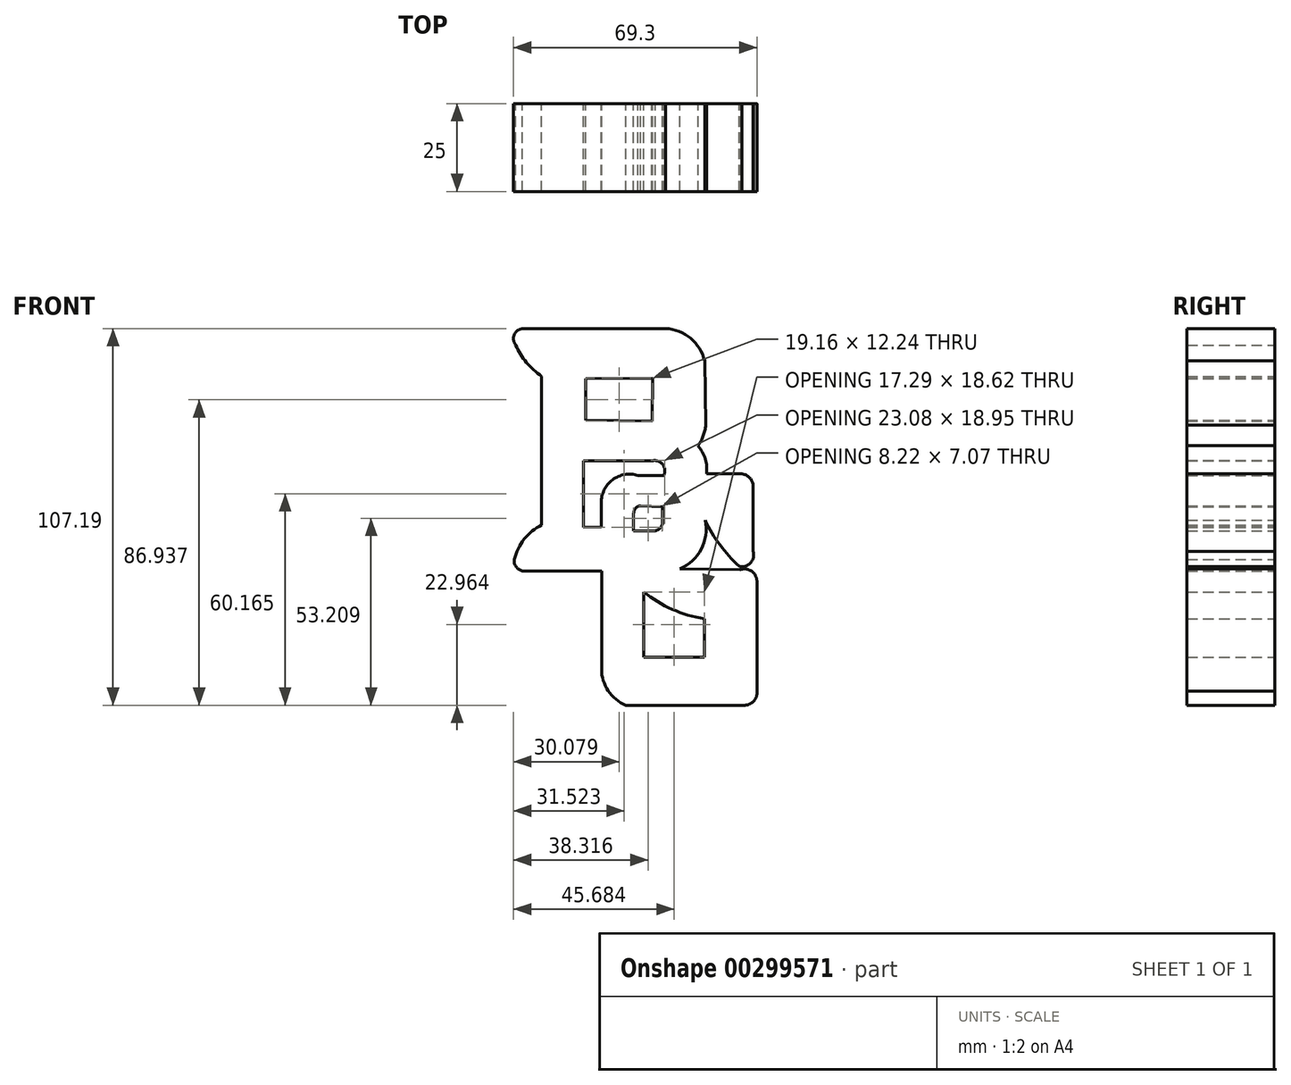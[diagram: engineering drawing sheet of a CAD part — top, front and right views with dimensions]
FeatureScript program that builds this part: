
annotation { "Feature Type Name" : "Feature", "Feature Type Description" : "" }
export const myFeature = defineFeature(function(context is Context, id is Id, definition is map)
    precondition{}
    {
        {
            var Q0;
            Q0=qCreatedBy(makeId("Front.planeOp"),FACE);
            var sketch = newSketch(context, id + "F0", { "sketchPlane" : qUnion([Q0])});
            skLineSegment(sketch, "E0", {"start": v(-27.36, 42.93) * mm, "end": v(-27.36, 0) * mm});
            skArc(sketch, "E1", {"start": v(-27.36, 0.63) * mm, "mid": v(-32.34, -3.42) * mm, "end": v(-35.18, -9.18) * mm});
            skArc(sketch, "E2", {"start": v(-35.18, -9.18) * mm, "mid": v(-34.67, -11.27) * mm, "end": v(-32.9, -12.48) * mm});
            skLineSegment(sketch, "E3", {"start": v(-32.9, -12.48) * mm, "end": v(-10.33, -12.48) * mm});
            skLineSegment(sketch, "E4", {"start": v(-10.33, -12.48) * mm, "end": v(-10.33, -40.36) * mm});
            skArc(sketch, "E5", {"start": v(-10.33, -40.36) * mm, "mid": v(-8.44, -46.58) * mm, "end": v(-3.41, -50.69) * mm});
            skLineSegment(sketch, "E6", {"start": v(-3.41, -50.69) * mm, "end": v(30.33, -50.69) * mm});
            skArc(sketch, "E7", {"start": v(30.33, -50.69) * mm, "mid": v(33.01, -49.48) * mm, "end": v(33.87, -46.66) * mm});
            skLineSegment(sketch, "E8", {"start": v(33.87, -46.66) * mm, "end": v(33.87, -15.42) * mm});
            skArc(sketch, "E9", {"start": v(33.87, -15.42) * mm, "mid": v(32.37, -12.54) * mm, "end": v(29.15, -12.12) * mm});
            skLineSegment(sketch, "E10", {"start": v(29.15, -12.12) * mm, "end": v(11.94, -11.88) * mm});
            skArc(sketch, "E11", {"start": v(11.94, -11.88) * mm, "mid": v(18.05, -6.3) * mm, "end": v(19.13, 1.91) * mm});
            skArc(sketch, "E12", {"start": v(19.13, 1.91) * mm, "mid": v(23.35, -5.06) * mm, "end": v(28.8, -11.14) * mm});
            skLineSegment(sketch, "E13", {"start": v(32.79, -6.95) * mm, "end": v(32.79, 11.61) * mm});
            skArc(sketch, "E14", {"start": v(32.79, 11.61) * mm, "mid": v(31.9, 13.96) * mm, "end": v(29.67, 15.13) * mm});
            skLineSegment(sketch, "E15", {"start": v(29.67, 15.13) * mm, "end": v(19.53, 15.13) * mm});
            skArc(sketch, "E16", {"start": v(19.53, 15.13) * mm, "mid": v(19.19, 19.39) * mm, "end": v(17.13, 23.14) * mm});
            skArc(sketch, "E17", {"start": v(17.13, 23.14) * mm, "mid": v(18.6, 25.95) * mm, "end": v(19.37, 29.03) * mm});
            skLineSegment(sketch, "E18", {"start": v(19.37, 29.03) * mm, "end": v(19.01, 47.3) * mm});
            skArc(sketch, "E19", {"start": v(19.01, 47.3) * mm, "mid": v(14.99, 53.73) * mm, "end": v(7.93, 56.5) * mm});
            skLineSegment(sketch, "E20", {"start": v(7.93, 56.5) * mm, "end": v(-32.51, 56.5) * mm});
            skArc(sketch, "E21", {"start": v(-32.51, 56.5) * mm, "mid": v(-35.12, 54.85) * mm, "end": v(-34.75, 51.79) * mm});
            skArc(sketch, "E22", {"start": v(-34.75, 51.79) * mm, "mid": v(-31.69, 46.83) * mm, "end": v(-27.36, 42.93) * mm});
            skLineSegment(sketch, "E23", {"start": v(-14.9, 42.2) * mm, "end": v(-14.9, 30.38) * mm});
            skLineSegment(sketch, "E24", {"start": v(-14.9, 30.38) * mm, "end": v(4.03, 30.13) * mm});
            skLineSegment(sketch, "E25", {"start": v(4.03, 30.13) * mm, "end": v(4.26, 42.37) * mm});
            skLineSegment(sketch, "E26", {"start": v(4.26, 42.37) * mm, "end": v(-14.9, 42.2) * mm});
            skLineSegment(sketch, "E27", {"start": v(-12.42, 10.1) * mm, "end": v(-12.49, 16.09) * mm});
            skLineSegment(sketch, "E28", {"start": v(-12.49, 16.09) * mm, "end": v(-6.72, 16.15) * mm});
            skArc(sketch, "E29", {"start": v(-6.72, 16.15) * mm, "mid": v(-10.19, 13.7) * mm, "end": v(-12.42, 10.1) * mm});
            skLineSegment(sketch, "E30", {"start": v(1.64, -18.42) * mm, "end": v(1.64, -37.03) * mm});
            skLineSegment(sketch, "E31", {"start": v(1.64, -37.03) * mm, "end": v(18.93, -37.03) * mm});
            skLineSegment(sketch, "E32", {"start": v(18.93, -37.03) * mm, "end": v(18.93, -26.1) * mm});
            skArc(sketch, "E33", {"start": v(1.64, -18.42) * mm, "mid": v(9.78, -23.39) * mm, "end": v(18.93, -26.1) * mm});
            skLineSegment(sketch, "E34", {"start": v(7.01, 5.83) * mm, "end": v(7.03, 1.42) * mm});
            skArc(sketch, "E35", {"start": v(5.01, -1.02) * mm, "mid": v(6.46, -0.17) * mm, "end": v(7.03, 1.42) * mm});
            skLineSegment(sketch, "E36", {"start": v(5.01, -1.02) * mm, "end": v(-1.2, -1.02) * mm});
            skLineSegment(sketch, "E37", {"start": v(-1.2, -1.02) * mm, "end": v(-1.2, 3.9) * mm});
            skArc(sketch, "E38", {"start": v(0.78, 6.06) * mm, "mid": v(-0.63, 5.37) * mm, "end": v(-1.2, 3.9) * mm});
            skLineSegment(sketch, "E39", {"start": v(0.78, 6.06) * mm, "end": v(7.01, 5.83) * mm});
            skLineSegment(sketch, "E40", {"start": v(-15.42, 18.83) * mm, "end": v(-15.42, 0) * mm});
            skLineSegment(sketch, "E41", {"start": v(-15.42, 0) * mm, "end": v(-10.35, 0.05) * mm});
            skLineSegment(sketch, "E42", {"start": v(-10.35, 0.05) * mm, "end": v(-10.42, 6.92) * mm});
            skArc(sketch, "E43", {"start": v(0, 14.74) * mm, "mid": v(-7.19, 13.47) * mm, "end": v(-10.42, 6.92) * mm});
            skLineSegment(sketch, "E44", {"start": v(0, 14.74) * mm, "end": v(7.42, 14.74) * mm});
            skArc(sketch, "E45", {"start": v(7.42, 14.74) * mm, "mid": v(6.98, 17.91) * mm, "end": v(3.9, 18.83) * mm});
            skLineSegment(sketch, "E46", {"start": v(3.9, 18.83) * mm, "end": v(-15.42, 18.83) * mm});
            skArc(sketch, "E47", {"start": v(28.8, -11.14) * mm, "mid": v(32.04, -10.23) * mm, "end": v(32.79, -6.95) * mm});
            skSolve(sketch);
        }
        {
            var Q0;
            Q0 = qSketchRegion(id + "F0", true);
            extrude(context, id + "F1", {"entities" : qUnion([Q0]), "depth" : 15 * mm});
        }
        {
            var Q0;
            Q0 = qSketchRegion(id + "F0", true);
            extrude(context, id + "F2", {"entities" : qUnion([Q0]), "operationType" : NewBodyOperationType.REMOVE, "endBound" : BoundingType.SYMMETRIC, "oppositeDirection" : true, "depth" : 5 * mm});
        }
        {
            var Q0;
            Q0 = qSketchRegion(id + "F0", true);
            extrude(context, id + "F3", {"entities" : qUnion([Q0]), "operationType" : NewBodyOperationType.ADD, "depth" : 25 * mm});
        }
    });
